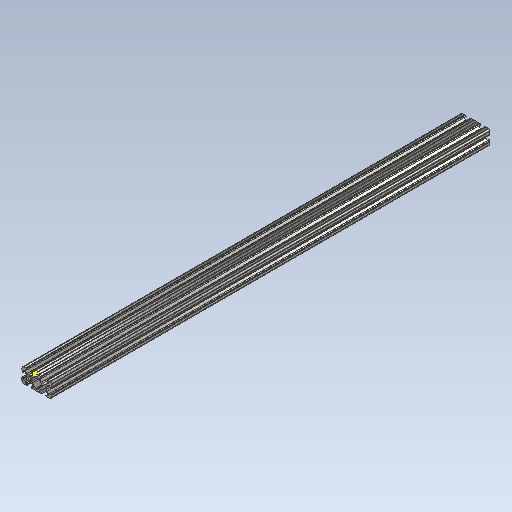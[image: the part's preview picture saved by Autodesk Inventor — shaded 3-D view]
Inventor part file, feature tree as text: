
AUTODESK INVENTOR PART (.ipt)
format: ipt  version: 2020 (Build 240168000, 168)  size: 399,872 bytes
history: native  units: in
note: dims shown in document units (in); Inventor stores cm internally (conversion verified against a paired STEP export)
features: other x3, sketch x2
ambient origin geometry x8: Origin, YZ Plane, XZ Plane, XY Plane, X Axis, Y Axis, Z Axis, Center Point
bodies: Solid1 (feature_tree)
feature tree (5):
  other  "25in 2x1 T Slot11.ipt"
  other  "Solid1::25in 2x1 T Slot11.ipt"
  other  "TaggingFeature1"
  sketch  "Sketch1"  dims[d0=0.3937in]
  sketch  "Sketch2"
